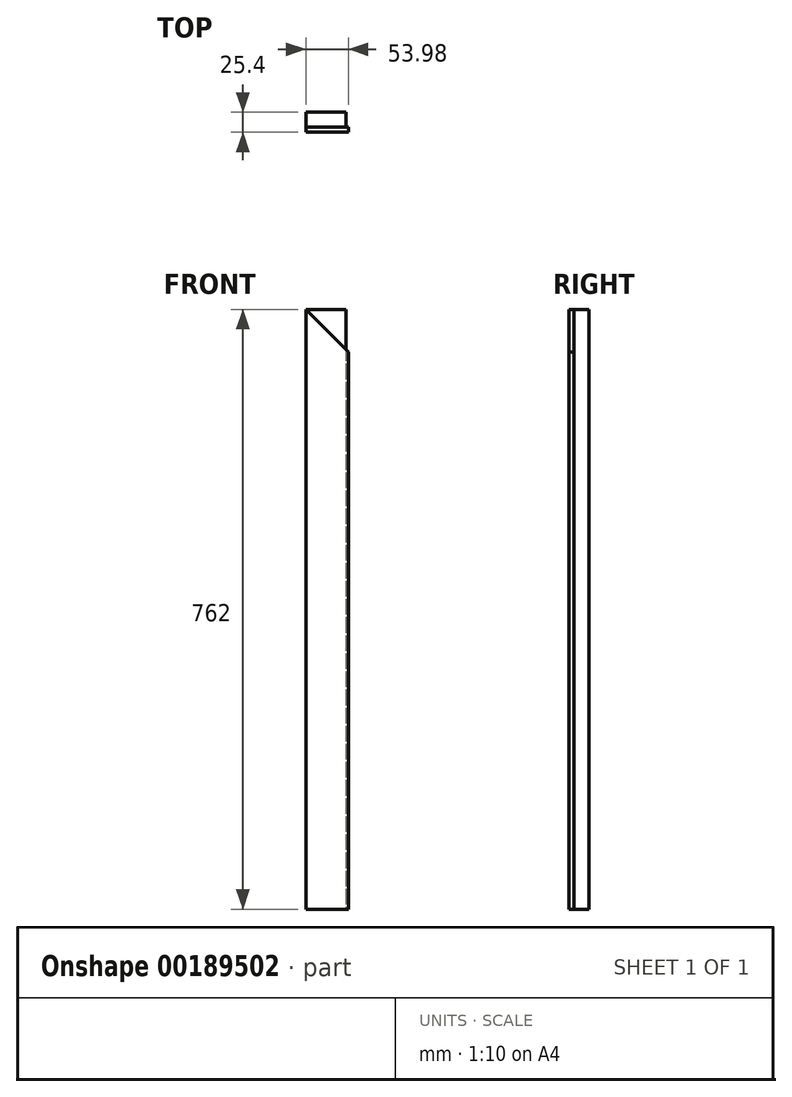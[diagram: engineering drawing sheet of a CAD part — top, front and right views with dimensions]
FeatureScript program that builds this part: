
annotation { "Feature Type Name" : "Feature", "Feature Type Description" : "" }
export const myFeature = defineFeature(function(context is Context, id is Id, definition is map)
    precondition{}
    {
        {
            var Q0;
            Q0=qCreatedBy(makeId("Top.planeOp"),FACE);
            var sketch = newSketch(context, id + "F0", { "sketchPlane" : qUnion([Q0])});
            skLineSegment(sketch, "E0.bottom", {"start": v(23.81, 12.7) * mm, "end": v(-26.99, 12.7) * mm});
            skLineSegment(sketch, "E0.top", {"start": v(26.99, -12.7) * mm, "end": v(-26.99, -12.7) * mm});
            skLineSegment(sketch, "E0.left", {"start": v(26.99, -6.35) * mm, "end": v(26.99, -12.7) * mm});
            skLineSegment(sketch, "E0.right", {"start": v(-26.99, 12.7) * mm, "end": v(-26.99, -12.7) * mm});
            skPoint(sketch, "E0.middle", {"position": v(0, 0) * mm});
            skLineSegment(sketch, "E1", {"start": v(26.99, -6.35) * mm, "end": v(23.81, -6.35) * mm});
            skLineSegment(sketch, "E2", {"start": v(23.81, -6.35) * mm, "end": v(23.81, 12.7) * mm});
            skPoint(sketch, "E3.orphan", {"position": v(26.99, 12.7) * mm});
            skSolve(sketch);
        }
        {
            var Q0;
            Q0 = qSketchRegion(id + "F0", true);
            extrude(context, id + "F1", {"entities" : qUnion([Q0]), "depth" : 762 * mm});
        }
        {
            var Q0;
            Q0=makeQuery(id+"F1.opExtrude","SWEPT_FACE",FACE,{"disambiguationData":[OSD([sQuery(id+"F0.wireOp",EDGE,"E0.top")])]});
            var sketch = newSketch(context, id + "F2", { "sketchPlane" : qUnion([Q0])});
            skLineSegment(sketch, "E4", {"start": v(-26.99, 762) * mm, "end": v(26.99, 708.03) * mm});
            skLineSegment(sketch, "E5", {"start": v(26.99, 708.03) * mm, "end": v(26.99, 762) * mm});
            skLineSegment(sketch, "E6", {"start": v(26.99, 762) * mm, "end": v(-26.99, 762) * mm});
            skSolve(sketch);
        }
        {
            var Q0;
            Q0 = qSketchRegion(id + "F2", true);
            extrude(context, id + "F3", {"entities" : qUnion([Q0]), "operationType" : NewBodyOperationType.REMOVE, "oppositeDirection" : true, "depth" : 6.35 * mm});
        }
    });
